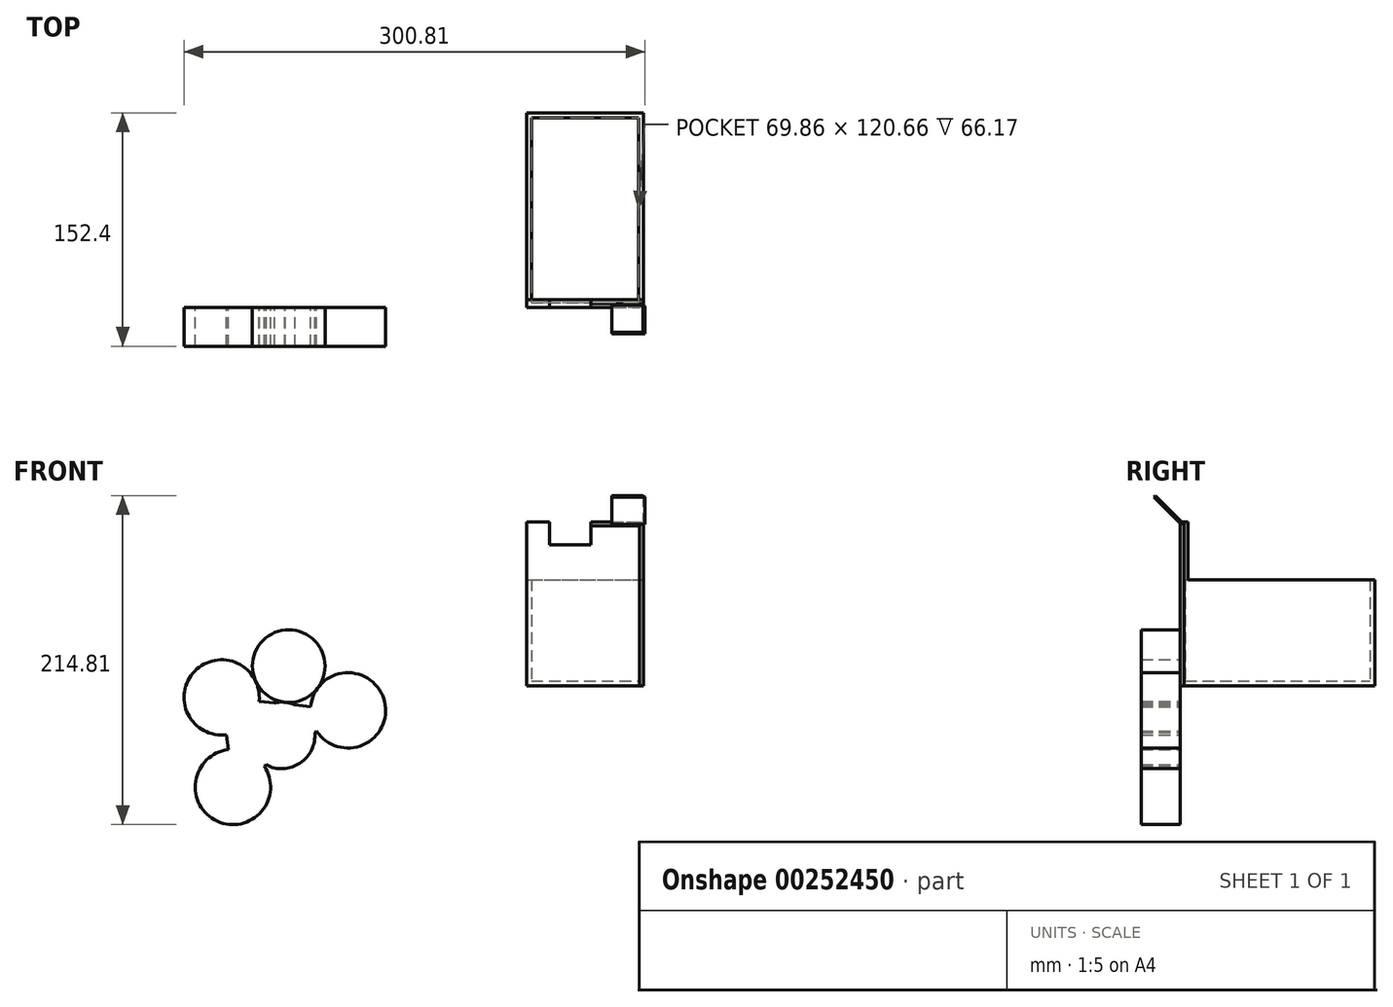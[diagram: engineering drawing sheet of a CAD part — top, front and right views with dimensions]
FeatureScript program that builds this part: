
annotation { "Feature Type Name" : "Feature", "Feature Type Description" : "" }
export const myFeature = defineFeature(function(context is Context, id is Id, definition is map)
    precondition{}
    {
        {
            var Q0;
            Q0=qCreatedBy(makeId("Top.planeOp"),FACE);
            var sketch = newSketch(context, id + "F0", { "sketchPlane" : qUnion([Q0])});
            skLineSegment(sketch, "E0.bottom", {"start": v(0, 0) * mm, "end": v(76.2, 0) * mm});
            skLineSegment(sketch, "E0.top", {"start": v(0, 127) * mm, "end": v(76.2, 127) * mm});
            skLineSegment(sketch, "E0.left", {"start": v(0, 0) * mm, "end": v(0, 127) * mm});
            skLineSegment(sketch, "E0.right", {"start": v(76.2, 0) * mm, "end": v(76.2, 127) * mm});
            skSolve(sketch);
        }
        {
            var Q0;
            Q0 = qSketchRegion(id + "F0", true);
            extrude(context, id + "F1", {"entities" : qUnion([Q0]), "depth" : 69.34 * mm, "offsetDistance" : 25.4 * mm});
        }
        {
            var Q0;
            Q0=makeQuery(id+"F1.opExtrude","SWEPT_FACE",FACE,{"disambiguationData":[OSD([sQuery(id+"F0.wireOp",EDGE,"E0.bottom")])]});
            var sketch = newSketch(context, id + "F2", { "sketchPlane" : qUnion([Q0])});
            skLineSegment(sketch, "E1.bottom", {"start": v(0, 69.34) * mm, "end": v(76.2, 69.34) * mm});
            skLineSegment(sketch, "E1.top", {"start": v(0, 107.18) * mm, "end": v(14.82, 107.18) * mm});
            skLineSegment(sketch, "E1.left", {"start": v(0, 69.34) * mm, "end": v(0, 107.18) * mm});
            skLineSegment(sketch, "E1.right", {"start": v(76.2, 69.34) * mm, "end": v(76.2, 107.18) * mm});
            skLineSegment(sketch, "E2.top", {"start": v(14.82, 92.2) * mm, "end": v(42.01, 92.2) * mm});
            skLineSegment(sketch, "E2.left", {"start": v(14.82, 107.18) * mm, "end": v(14.82, 92.2) * mm});
            skLineSegment(sketch, "E2.right", {"start": v(42.01, 107.18) * mm, "end": v(42.01, 92.2) * mm});
            skLineSegment(sketch, "E3.trimOffspring", {"start": v(42.01, 107.18) * mm, "end": v(76.2, 107.18) * mm});
            skSolve(sketch);
        }
        {
            var Q0;
            Q0 = qSketchRegion(id + "F2", true);
            extrude(context, id + "F3", {"entities" : qUnion([Q0]), "operationType" : NewBodyOperationType.ADD, "oppositeDirection" : true, "depth" : 5.08 * mm});
        }
        {
            var Q0;
            Q0=makeQuery(id+"F1.opExtrude","CAP_FACE",FACE,{"disambiguationData":[OSD([sQuery(id+"F0.wireOp",EDGE,"E0.bottom"),sQuery(id+"F0.wireOp",EDGE,"E0.top"),sQuery(id+"F0.wireOp",EDGE,"E0.left"),sQuery(id+"F0.wireOp",EDGE,"E0.right")])],"isStart":false});
            shell(context, id + "F4", {"entities" : qUnion([Q0]), "thickness" : 3.17 * mm});
        }
        {
            var Q0;
            Q0=makeQuery(id+"F3.boolean.opBoolean","MERGE",FACE,{"derivedFrom":[makeQuery(id+"F1.opExtrude","SWEPT_FACE",FACE,{"disambiguationData":[OSD([sQuery(id+"F0.wireOp",EDGE,"E0.bottom")])]}),makeQuery(id+"F3.opExtrude","CAP_FACE",FACE,{"disambiguationData":[OSD([sQuery(id+"F2.wireOp",EDGE,"E1.bottom"),sQuery(id+"F2.wireOp",EDGE,"E1.top"),sQuery(id+"F2.wireOp",EDGE,"E1.left"),sQuery(id+"F2.wireOp",EDGE,"E1.right"),sQuery(id+"F2.wireOp",EDGE,"E2.top"),sQuery(id+"F2.wireOp",EDGE,"E2.left"),sQuery(id+"F2.wireOp",EDGE,"E2.right"),sQuery(id+"F2.wireOp",EDGE,"E3.trimOffspring")])],"isStart":true})]});
            var sketch = newSketch(context, id + "F5", { "sketchPlane" : qUnion([Q0])});
            skCircle(sketch, "E4", {"center": v(-198.96, -7.5) * mm, "radius": 24.57 * mm});
            skCircle(sketch, "E5", {"center": v(-191.63, -66) * mm, "radius": 24.57 * mm});
            skCircle(sketch, "E6", {"center": v(-116.5, -15.98) * mm, "radius": 24.57 * mm});
            skLineSegment(sketch, "E7", {"start": v(-198.96, -7.5) * mm, "end": v(-116.5, -15.98) * mm});
            skLineSegment(sketch, "E8", {"start": v(-198.96, -7.5) * mm, "end": v(-191.63, -66) * mm});
            skLineSegment(sketch, "E9", {"start": v(-191.63, -66) * mm, "end": v(-116.5, -15.98) * mm});
            skCircle(sketch, "E10", {"center": v(-159.85, -32.3) * mm, "radius": 21.74 * mm});
            skCircle(sketch, "E11", {"center": v(-155.2, 12.9) * mm, "radius": 23.7 * mm});
            skSolve(sketch);
        }
        {
            var Q0;
            Q0 = qSketchRegion(id + "F5", true);
            extrude(context, id + "F6", {"entities" : qUnion([Q0]), "operationType" : NewBodyOperationType.ADD, "depth" : 25.4 * mm, "offsetDistance" : 25.4 * mm});
        }
        {
            var Q0;
            Q0=makeQuery(id+"F3.opExtrude","CAP_EDGE",EDGE,{"disambiguationData":[OSD([sQuery(id+"F2.wireOp",EDGE,"E3.trimOffspring")])],"isStart":true});
            var Q1;
            Q1=makeQuery(id+"F3.boolean.opBoolean","MERGE",EDGE,{"derivedFrom":[makeQuery(id+"F1.opExtrude","SWEPT_EDGE",EDGE,{"disambiguationData":[OSD([sQuery(id+"F0.wireOp",EDGE,"E0.bottom"),sQuery(id+"F0.wireOp",EDGE,"E0.right")])]}),makeQuery(id+"F3.opExtrude","CAP_EDGE",EDGE,{"disambiguationData":[OSD([sQuery(id+"F2.wireOp",EDGE,"E1.right")])],"isStart":true})]});
            chamfer(context, id + "F7", {"entities" : qUnion([Q0, Q1]), "width" : 2.54 * mm, "tangentPropagation" : true});
        }
        {
            var Q0;
            Q0=makeQuery(id+"F7.opChamfer","BLEND_FACE",FACE,{"disambiguationData":[OSD([sQuery(id+"F2.wireOp",EDGE,"E3.trimOffspring")])]});
            var sketch = newSketch(context, id + "F8", { "sketchPlane" : qUnion([Q0])});
            skLineSegment(sketch, "E12.bottom", {"start": v(55.69, 76.31) * mm, "end": v(81.09, 76.31) * mm});
            skLineSegment(sketch, "E12.top", {"start": v(55.69, 75.04) * mm, "end": v(81.09, 75.04) * mm});
            skLineSegment(sketch, "E12.left", {"start": v(55.69, 76.31) * mm, "end": v(55.69, 75.04) * mm});
            skLineSegment(sketch, "E12.right", {"start": v(81.09, 76.31) * mm, "end": v(81.09, 75.04) * mm});
            skSolve(sketch);
        }
        {
            var Q0;
            Q0 = qSketchRegion(id + "F8", true);
            extrude(context, id + "F9", {"entities" : qUnion([Q0]), "operationType" : NewBodyOperationType.ADD, "depth" : 25.4 * mm, "offsetDistance" : 25.4 * mm});
        }
        {
            var Q0;
            Q0=makeQuery(id+"F9.opExtrude","SWEPT_EDGE",EDGE,{"disambiguationData":[OSD([sQuery(id+"F8.wireOp",EDGE,"E12.bottom"),sQuery(id+"F8.wireOp",EDGE,"E12.right")])]});
            chamfer(context, id + "F10", {"entities" : qUnion([Q0]), "width" : 5.08 * mm, "tangentPropagation" : true});
        }
    });
